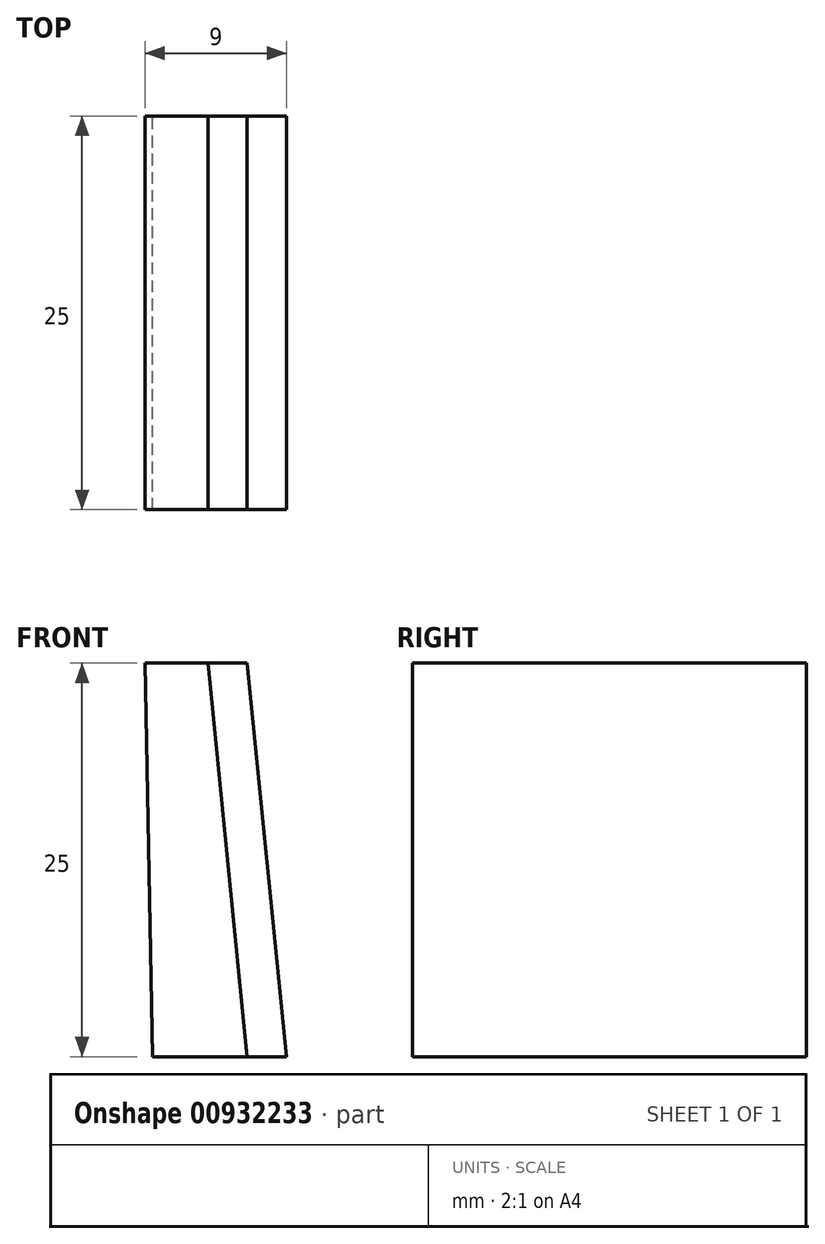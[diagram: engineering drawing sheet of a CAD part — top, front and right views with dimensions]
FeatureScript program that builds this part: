
annotation { "Feature Type Name" : "Feature", "Feature Type Description" : "" }
export const myFeature = defineFeature(function(context is Context, id is Id, definition is map)
    precondition{}
    {
        {
            var Q0;
            Q0=qCreatedBy(makeId("Front.planeOp"),FACE);
            var sketch = newSketch(context, id + "F0", { "sketchPlane" : qUnion([Q0])});
            skLineSegment(sketch, "E0.bottom", {"start": v(2.25, -12.5) * mm, "end": v(-1.75, -12.5) * mm});
            skLineSegment(sketch, "E0.top", {"start": v(1.75, 12.5) * mm, "end": v(-2.25, 12.5) * mm});
            skLineSegment(sketch, "E0.left", {"start": v(2.25, -12.5) * mm, "end": v(1.75, 12.5) * mm});
            skLineSegment(sketch, "E0.right", {"start": v(-1.75, -12.5) * mm, "end": v(-2.25, 12.5) * mm});
            skPoint(sketch, "E0.middle", {"position": v(0, 0) * mm});
            skLineSegment(sketch, "E1", {"start": v(1.75, 12.5) * mm, "end": v(4.25, -12.5) * mm});
            skLineSegment(sketch, "E2", {"start": v(4.25, -12.5) * mm, "end": v(2.25, -12.5) * mm});
            skLineSegment(sketch, "E3", {"start": v(4.25, -12.5) * mm, "end": v(6.75, -12.5) * mm});
            skLineSegment(sketch, "E4", {"start": v(6.75, -12.5) * mm, "end": v(4.25, 12.5) * mm});
            skLineSegment(sketch, "E5", {"start": v(4.25, 12.5) * mm, "end": v(1.75, 12.5) * mm});
            skSolve(sketch);
        }
        {
            var Q0;
            Q0=makeQuery(id+"F0.imprint","IMPRINT",FACE,{"disambiguationData":[TD([[makeQuery(id+"F0.imprint","IMPRINT",EDGE,{"derivedFrom":sQuery(id+"F0.wireOp",EDGE,"E0.left")}),-1.0]])]});
            var Q1;
            Q1=makeQuery(id+"F0.imprint","IMPRINT",FACE,{"disambiguationData":[TD([[makeQuery(id+"F0.imprint","IMPRINT",EDGE,{"derivedFrom":sQuery(id+"F0.wireOp",EDGE,"E0.bottom")}),-1.0]])]});
            extrude(context, id + "F1", {"entities" : qUnion([Q0, Q1]), "depth" : 25 * mm, "offsetDistance" : 25 * mm});
        }
        {
            var Q0;
            Q0=makeQuery(id+"F0.imprint","IMPRINT",FACE,{"disambiguationData":[TD([[makeQuery(id+"F0.imprint","IMPRINT",EDGE,{"derivedFrom":sQuery(id+"F0.wireOp",EDGE,"E1")}),1.0]])]});
            extrude(context, id + "F2", {"entities" : qUnion([Q0]), "depth" : 25 * mm, "offsetDistance" : 25 * mm});
        }
    });
